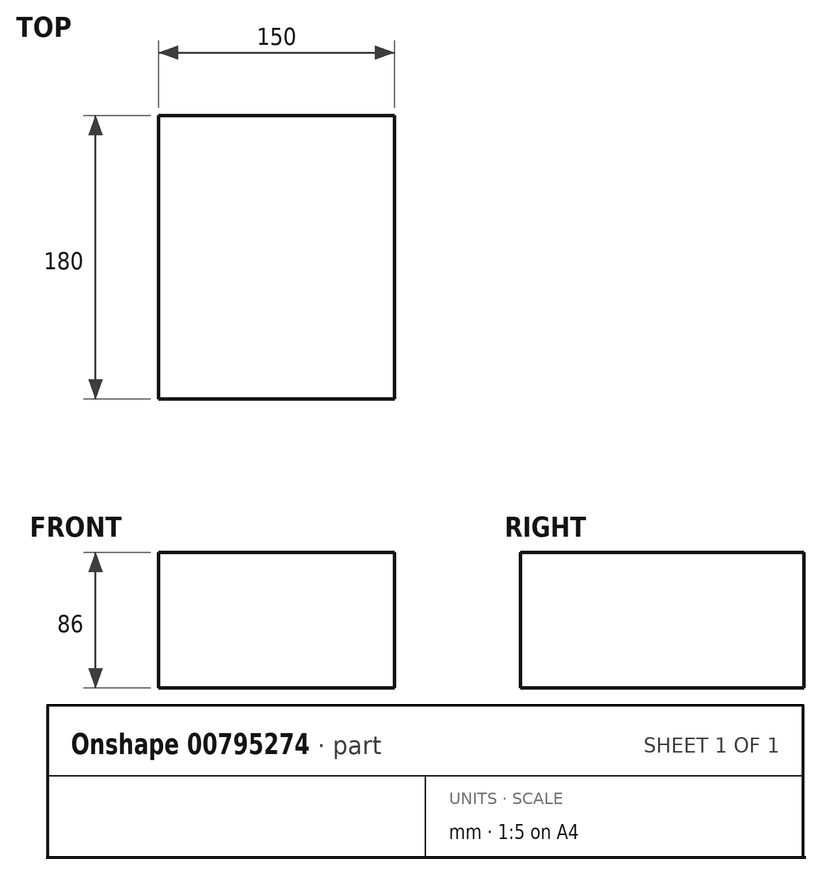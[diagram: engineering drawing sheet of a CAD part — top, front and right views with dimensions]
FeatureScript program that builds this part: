
annotation { "Feature Type Name" : "Feature", "Feature Type Description" : "" }
export const myFeature = defineFeature(function(context is Context, id is Id, definition is map)
    precondition{}
    {
        {
            var Q0;
            Q0=qCreatedBy(makeId("Front.planeOp"),FACE);
            var sketch = newSketch(context, id + "F0", { "sketchPlane" : qUnion([Q0])});
            skLineSegment(sketch, "E0.bottom", {"start": v(75, -43) * mm, "end": v(-75, -43) * mm});
            skLineSegment(sketch, "E0.top", {"start": v(75, 43) * mm, "end": v(-75, 43) * mm});
            skLineSegment(sketch, "E0.left", {"start": v(75, -43) * mm, "end": v(75, 43) * mm});
            skLineSegment(sketch, "E0.right", {"start": v(-75, -43) * mm, "end": v(-75, 43) * mm});
            skPoint(sketch, "E0.middle", {"position": v(0, 0) * mm});
            skSolve(sketch);
        }
        {
            var Q0;
            Q0 = qSketchRegion(id + "F0", true);
            extrude(context, id + "F1", {"entities" : qUnion([Q0]), "oppositeDirection" : true, "depth" : 180 * mm, "offsetDistance" : 25.4 * mm});
        }
    });
